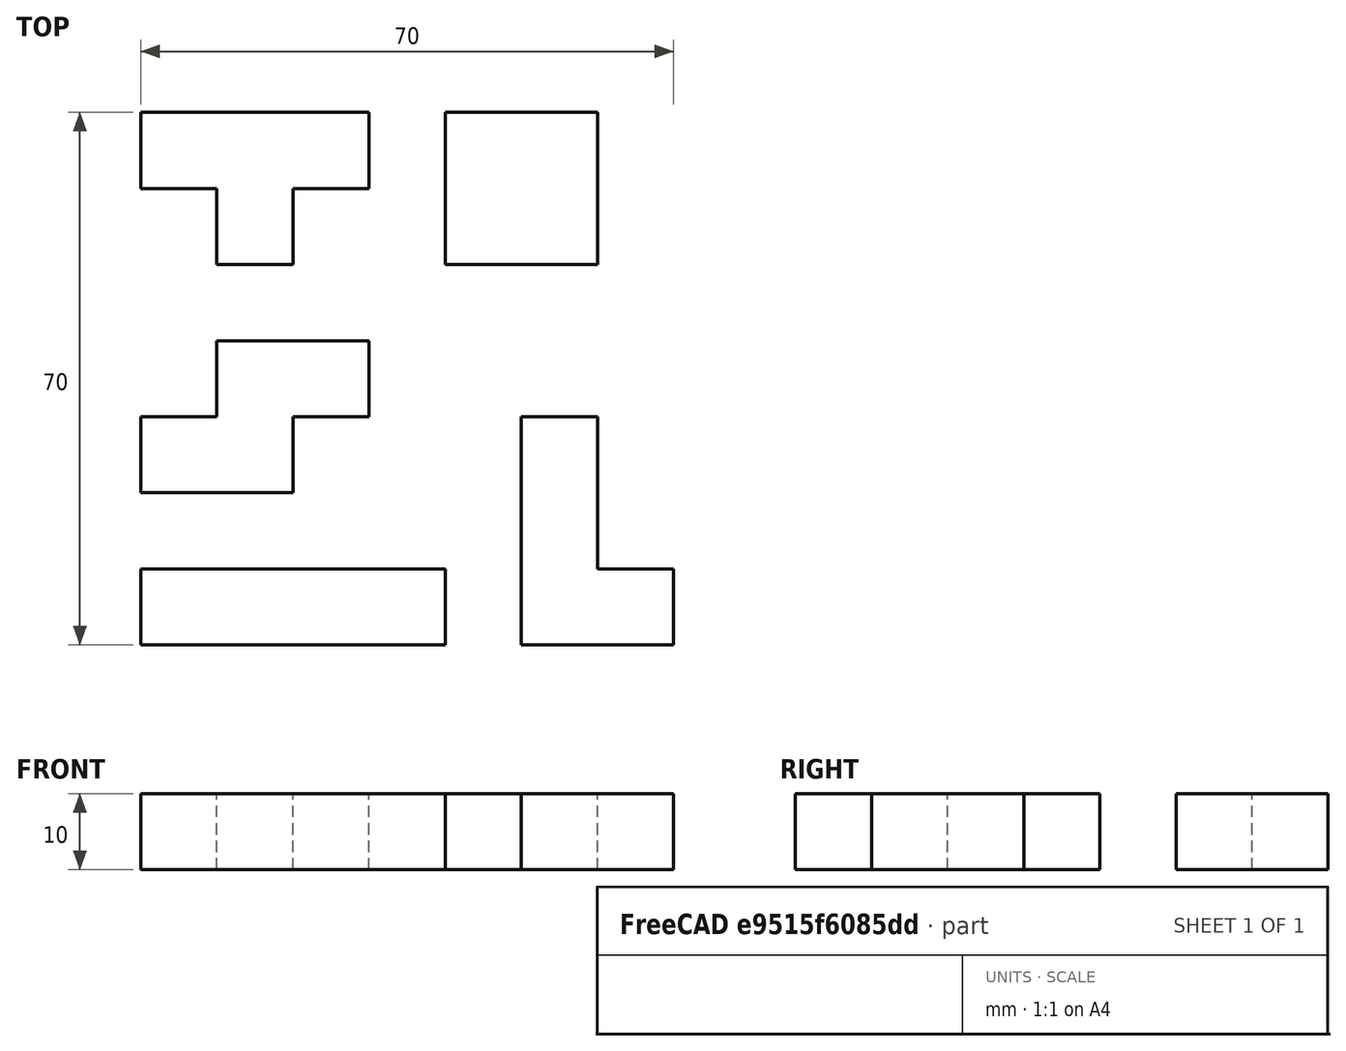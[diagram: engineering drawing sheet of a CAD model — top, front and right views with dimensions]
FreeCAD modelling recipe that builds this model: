
FCSTD DOCUMENT  (FreeCAD 1.0R39319 (Git))
Label: ojt1_t05_r03_tetris
License: All rights reserved
LicenseURL: https://en.wikipedia.org/wiki/All_rights_reserved
objects: Part::Box×8, Part::MultiFuse×3
note: 11 computed .brp shape members not serialized (recipe doc carries the construction recipe); baked Part::Feature solids carry a one-line shape summary decoded from their .brp

FEATURE [Part::Box] Box  label="Cubo"
  AttacherType = Attacher::AttachEngine3D
  Height = 10
  Length = 40
  Width = 10
FEATURE [Part::Box] Box001  label="Cubo001"
  AttacherType = Attacher::AttachEngine3D
  Height = 10
  Length = 20
  Placement = pos=(0,20,0) rot=(0,0,1;0rad)
  Width = 10
FEATURE [Part::Box] Box002  label="Cubo002"
  AttacherType = Attacher::AttachEngine3D
  Height = 10
  Length = 20
  Placement = pos=(10,30,0) rot=(0,0,1;0rad)
  Width = 10
FEATURE [Part::MultiFuse] Fusion
  Refine = true
  Shapes = -> [Box002,Box001]
FEATURE [Part::Box] Box003  label="Cubo003"
  AttacherType = Attacher::AttachEngine3D
  Height = 10
  Length = 10
  Placement = pos=(10,50,0) rot=(0,0,1;0rad)
  Width = 10
FEATURE [Part::Box] Box004  label="Cubo004"
  AttacherType = Attacher::AttachEngine3D
  Height = 10
  Length = 30
  Placement = pos=(0,60,0) rot=(0,0,1;0rad)
  Width = 10
FEATURE [Part::MultiFuse] Fusion001
  Refine = true
  Shapes = -> [Box004,Box003]
FEATURE [Part::Box] Box005  label="Cubo005"
  AttacherType = Attacher::AttachEngine3D
  Height = 10
  Length = 20
  Placement = pos=(40,50,0) rot=(0,0,1;0rad)
  Width = 20
FEATURE [Part::Box] Box006  label="Cubo006"
  AttacherType = Attacher::AttachEngine3D
  Height = 10
  Length = 20
  Placement = pos=(50,0,0) rot=(0,0,1;0rad)
  Width = 10
FEATURE [Part::Box] Box007  label="Cubo007"
  AttacherType = Attacher::AttachEngine3D
  Height = 10
  Length = 10
  Placement = pos=(50,0,0) rot=(0,0,1;0rad)
  Width = 30
FEATURE [Part::MultiFuse] Fusion002
  Refine = true
  Shapes = -> [Box007,Box006]
